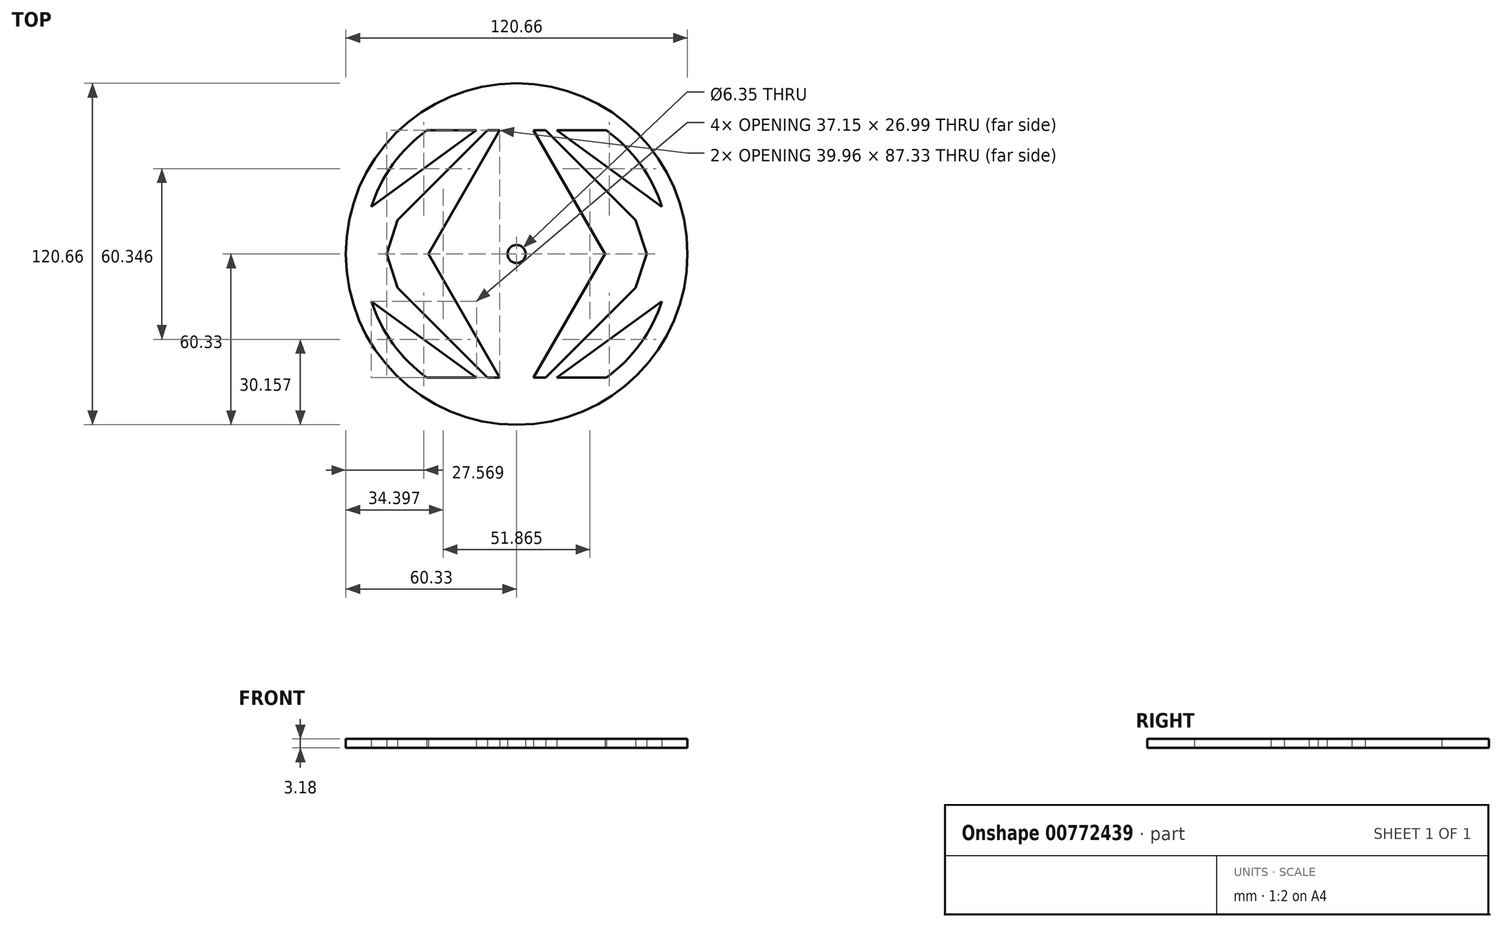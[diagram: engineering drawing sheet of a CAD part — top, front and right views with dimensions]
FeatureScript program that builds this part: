
annotation { "Feature Type Name" : "Feature", "Feature Type Description" : "" }
export const myFeature = defineFeature(function(context is Context, id is Id, definition is map)
    precondition{}
    {
        {
            var Q0;
            Q0=qCreatedBy(makeId("Top.planeOp"),FACE);
            var sketch = newSketch(context, id + "F0", { "sketchPlane" : qUnion([Q0])});
            skCircle(sketch, "E0", {"center": v(0, 0) * mm, "radius": 60.32 * mm});
            skCircle(sketch, "E1.0", {"center": v(0, 0) * mm, "radius": 53.97 * mm});
            skCircle(sketch, "E2.cCircle", {"center": v(0, 0) * mm, "radius": 53.97 * mm, "construction": true});
            skLineSegment(sketch, "E2.0", {"start": v(0, 53.97) * mm, "end": v(51.33, 16.68) * mm});
            skLineSegment(sketch, "E2.1", {"start": v(51.33, 16.68) * mm, "end": v(31.73, -43.67) * mm});
            skLineSegment(sketch, "E2.2", {"start": v(31.73, -43.67) * mm, "end": v(-31.73, -43.67) * mm});
            skLineSegment(sketch, "E2.3", {"start": v(-31.73, -43.67) * mm, "end": v(-51.33, 16.68) * mm});
            skLineSegment(sketch, "E2.4", {"start": v(-51.33, 16.68) * mm, "end": v(0, 53.97) * mm});
            skLineSegment(sketch, "E3.0", {"start": v(0, 53.97) * mm, "end": v(53.97, 0) * mm});
            skLineSegment(sketch, "E3.1", {"start": v(53.98, 0) * mm, "end": v(0, -53.97) * mm});
            skLineSegment(sketch, "E3.2", {"start": v(0, -53.97) * mm, "end": v(-53.97, 0) * mm});
            skLineSegment(sketch, "E3.3", {"start": v(-53.97, 0) * mm, "end": v(0, 53.97) * mm});
            skLineSegment(sketch, "E4.0", {"start": v(0, 53.97) * mm, "end": v(46.74, -26.99) * mm});
            skLineSegment(sketch, "E4.1", {"start": v(46.74, -26.99) * mm, "end": v(-46.74, -26.99) * mm});
            skLineSegment(sketch, "E4.2", {"start": v(-46.74, -26.99) * mm, "end": v(0, 53.98) * mm});
            skLineSegment(sketch, "E5.0", {"start": v(0, -53.97) * mm, "end": v(-51.33, -16.68) * mm});
            skLineSegment(sketch, "E5.1", {"start": v(-51.33, -16.68) * mm, "end": v(-31.73, 43.67) * mm});
            skLineSegment(sketch, "E5.2", {"start": v(-31.73, 43.67) * mm, "end": v(31.73, 43.67) * mm});
            skLineSegment(sketch, "E5.3", {"start": v(31.73, 43.67) * mm, "end": v(51.33, -16.68) * mm});
            skLineSegment(sketch, "E5.4", {"start": v(51.33, -16.68) * mm, "end": v(0, -53.97) * mm});
            skLineSegment(sketch, "E6.1", {"start": v(-53.98, 0) * mm, "end": v(0, 53.98) * mm});
            skLineSegment(sketch, "E6.3", {"start": v(53.97, 0) * mm, "end": v(0, -53.97) * mm});
            skLineSegment(sketch, "E7.0", {"start": v(0, -53.97) * mm, "end": v(-46.74, 26.99) * mm});
            skLineSegment(sketch, "E7.1", {"start": v(-46.74, 26.99) * mm, "end": v(46.74, 26.99) * mm});
            skLineSegment(sketch, "E7.2", {"start": v(46.74, 26.99) * mm, "end": v(0, -53.97) * mm});
            skCircle(sketch, "E8", {"center": v(0, 0) * mm, "radius": 3.18 * mm});
            skSolve(sketch);
        }
        {
            var Q0;
            Q0=makeQuery(id+"F0.imprint","IMPRINT",FACE,{"disambiguationData":[TD([[makeQuery(id+"F0.imprint","IMPRINT",EDGE,{"derivedFrom":sQuery(id+"F0.wireOp",EDGE,"E0")}),1.0]])]});
            var Q1;
            {var subQ0=sQuery(id+"F0.wireOp",EDGE,"E5.2");var subQ1=sQuery(id+"F0.wireOp",EDGE,"E2.0");var subQ2=makeQuery(id+"F0.imprint","INTERSECT",VERTEX,{"derivedFrom":[subQ1,subQ0]});Q1=makeQuery(id+"F0.imprint","IMPRINT",FACE,{"disambiguationData":[TD([[makeQuery(id+"F0.imprint","IMPRINT",EDGE,{"disambiguationData":[TD([[subQ2,1.0]])],"derivedFrom":subQ0}),-1.0]])]});}
            var Q2;
            {var subQ1=sQuery(id+"F0.wireOp",EDGE,"E2.0");var subQ3=sQuery(id+"F0.wireOp",EDGE,"E5.2");var subQ4=makeQuery(id+"F0.imprint","INTERSECT",VERTEX,{"derivedFrom":[subQ1,subQ3]});Q2=makeQuery(id+"F0.imprint","IMPRINT",FACE,{"disambiguationData":[TD([[makeQuery(id+"F0.imprint","IMPRINT",EDGE,{"disambiguationData":[TD([[subQ4,1.0]])],"derivedFrom":subQ3}),1.0]])]});}
            var Q3;
            {var subQ3=sQuery(id+"F0.wireOp",EDGE,"E7.1");var subQ5=sQuery(id+"F0.wireOp",EDGE,"E3.0");var subQ6=makeQuery(id+"F0.imprint","INTERSECT",VERTEX,{"derivedFrom":[subQ5,subQ3]});Q3=makeQuery(id+"F0.imprint","IMPRINT",FACE,{"disambiguationData":[TD([[makeQuery(id+"F0.imprint","IMPRINT",EDGE,{"disambiguationData":[TD([[subQ6,-1.0]])],"derivedFrom":subQ5}),1.0]])]});}
            var Q4;
            {var subQ0=sQuery(id+"F0.wireOp",EDGE,"E7.2");var subQ1=sQuery(id+"F0.wireOp",EDGE,"E2.0");var subQ2=makeQuery(id+"F0.imprint","INTERSECT",VERTEX,{"derivedFrom":[subQ1,subQ0]});Q4=makeQuery(id+"F0.imprint","IMPRINT",FACE,{"disambiguationData":[TD([[makeQuery(id+"F0.imprint","IMPRINT",EDGE,{"disambiguationData":[TD([[subQ2,-1.0]])],"derivedFrom":subQ0}),-1.0]])]});}
            var Q5;
            {var subQ0=sQuery(id+"F0.wireOp",EDGE,"E7.2");var subQ1=sQuery(id+"F0.wireOp",EDGE,"E5.3");var subQ2=makeQuery(id+"F0.imprint","INTERSECT",VERTEX,{"derivedFrom":[subQ1,subQ0]});Q5=makeQuery(id+"F0.imprint","IMPRINT",FACE,{"disambiguationData":[TD([[makeQuery(id+"F0.imprint","IMPRINT",EDGE,{"disambiguationData":[TD([[subQ2,-1.0]])],"derivedFrom":subQ1}),-1.0]])]});}
            var Q6;
            {var subQ3=sQuery(id+"F0.wireOp",EDGE,"E5.3");var subQ7=sQuery(id+"F0.wireOp",EDGE,"E7.2");var subQ9=makeQuery(id+"F0.imprint","INTERSECT",VERTEX,{"derivedFrom":[subQ3,subQ7]});Q6=makeQuery(id+"F0.imprint","IMPRINT",FACE,{"disambiguationData":[TD([[makeQuery(id+"F0.imprint","IMPRINT",EDGE,{"disambiguationData":[TD([[subQ9,-1.0]])],"derivedFrom":subQ3}),1.0]])]});}
            var Q7;
            {var subQ0=sQuery(id+"F0.wireOp",EDGE,"E2.1");var subQ3=sQuery(id+"F0.wireOp",EDGE,"E3.0");var subQ5=makeQuery(id+"F0.imprint","INTERSECT",VERTEX,{"derivedFrom":[subQ0,subQ3]});Q7=makeQuery(id+"F0.imprint","IMPRINT",FACE,{"disambiguationData":[TD([[makeQuery(id+"F0.imprint","IMPRINT",EDGE,{"disambiguationData":[TD([[subQ5,1.0]])],"derivedFrom":subQ0}),1.0]])]});}
            var Q8;
            {var subQ0=sQuery(id+"F0.wireOp",EDGE,"E3.0");var subQ1=sQuery(id+"F0.wireOp",EDGE,"E2.1");var subQ2=makeQuery(id+"F0.imprint","INTERSECT",VERTEX,{"derivedFrom":[subQ1,subQ0]});Q8=makeQuery(id+"F0.imprint","IMPRINT",FACE,{"disambiguationData":[TD([[makeQuery(id+"F0.imprint","IMPRINT",EDGE,{"disambiguationData":[TD([[subQ2,-1.0]])],"derivedFrom":subQ1}),1.0]])]});}
            var Q9;
            {var subQ0=sQuery(id+"F0.wireOp",EDGE,"E5.3");var subQ3=sQuery(id+"F0.wireOp",EDGE,"E6.3");var subQ5=makeQuery(id+"F0.imprint","INTERSECT",VERTEX,{"derivedFrom":[subQ0,subQ3]});Q9=makeQuery(id+"F0.imprint","IMPRINT",FACE,{"disambiguationData":[TD([[makeQuery(id+"F0.imprint","IMPRINT",EDGE,{"disambiguationData":[TD([[subQ5,-1.0]])],"derivedFrom":subQ0}),1.0]])]});}
            var Q10;
            {var subQ5=sQuery(id+"F0.wireOp",EDGE,"E6.3");var subQ7=sQuery(id+"F0.wireOp",EDGE,"E2.1");var subQ9=makeQuery(id+"F0.imprint","INTERSECT",VERTEX,{"derivedFrom":[subQ7,subQ5]});Q10=makeQuery(id+"F0.imprint","IMPRINT",FACE,{"disambiguationData":[TD([[makeQuery(id+"F0.imprint","IMPRINT",EDGE,{"disambiguationData":[TD([[subQ9,-1.0]])],"derivedFrom":subQ7}),1.0]])]});}
            var Q11;
            {var subQ0=sQuery(id+"F0.wireOp",EDGE,"E4.0");var subQ1=sQuery(id+"F0.wireOp",EDGE,"E2.1");var subQ2=makeQuery(id+"F0.imprint","INTERSECT",VERTEX,{"derivedFrom":[subQ1,subQ0]});Q11=makeQuery(id+"F0.imprint","IMPRINT",FACE,{"disambiguationData":[TD([[makeQuery(id+"F0.imprint","IMPRINT",EDGE,{"disambiguationData":[TD([[subQ2,-1.0]])],"derivedFrom":subQ0}),-1.0]])]});}
            var Q12;
            {var subQ0=sQuery(id+"F0.wireOp",EDGE,"E4.0");var subQ1=sQuery(id+"F0.wireOp",EDGE,"E2.1");var subQ2=makeQuery(id+"F0.imprint","INTERSECT",VERTEX,{"derivedFrom":[subQ1,subQ0]});Q12=makeQuery(id+"F0.imprint","IMPRINT",FACE,{"disambiguationData":[TD([[makeQuery(id+"F0.imprint","IMPRINT",EDGE,{"disambiguationData":[TD([[subQ2,1.0]])],"derivedFrom":subQ0}),-1.0]])]});}
            var Q13;
            {var subQ0=sQuery(id+"F0.wireOp",EDGE,"E5.4");var subQ1=sQuery(id+"F0.wireOp",EDGE,"E2.2");var subQ2=makeQuery(id+"F0.imprint","INTERSECT",VERTEX,{"derivedFrom":[subQ1,subQ0]});Q13=makeQuery(id+"F0.imprint","IMPRINT",FACE,{"disambiguationData":[TD([[makeQuery(id+"F0.imprint","IMPRINT",EDGE,{"disambiguationData":[TD([[subQ2,-1.0]])],"derivedFrom":subQ1}),-1.0]])]});}
            var Q14;
            {var subQ0=sQuery(id+"F0.wireOp",EDGE,"E5.4");var subQ1=sQuery(id+"F0.wireOp",EDGE,"E2.2");var subQ2=makeQuery(id+"F0.imprint","INTERSECT",VERTEX,{"derivedFrom":[subQ1,subQ0]});Q14=makeQuery(id+"F0.imprint","IMPRINT",FACE,{"disambiguationData":[TD([[makeQuery(id+"F0.imprint","IMPRINT",EDGE,{"disambiguationData":[TD([[subQ2,-1.0]])],"derivedFrom":subQ1}),1.0]])]});}
            var Q15;
            {var subQ0=sQuery(id+"F0.wireOp",EDGE,"E6.3");var subQ1=sQuery(id+"F0.wireOp",EDGE,"E2.1");var subQ2=makeQuery(id+"F0.imprint","INTERSECT",VERTEX,{"derivedFrom":[subQ1,subQ0]});Q15=makeQuery(id+"F0.imprint","IMPRINT",FACE,{"disambiguationData":[TD([[makeQuery(id+"F0.imprint","IMPRINT",EDGE,{"disambiguationData":[TD([[subQ2,-1.0]])],"derivedFrom":subQ1}),-1.0]])]});}
            var Q16;
            {var subQ0=sQuery(id+"F0.wireOp",EDGE,"E3.0");var subQ1=sQuery(id+"F0.wireOp",EDGE,"E2.1");var subQ2=makeQuery(id+"F0.imprint","INTERSECT",VERTEX,{"derivedFrom":[subQ1,subQ0]});Q16=makeQuery(id+"F0.imprint","IMPRINT",FACE,{"disambiguationData":[TD([[makeQuery(id+"F0.imprint","IMPRINT",EDGE,{"disambiguationData":[TD([[subQ2,-1.0]])],"derivedFrom":subQ1}),-1.0]])]});}
            var Q17;
            {var subQ0=sQuery(id+"F0.wireOp",EDGE,"E5.3");var subQ1=sQuery(id+"F0.wireOp",EDGE,"E2.1");var subQ2=makeQuery(id+"F0.imprint","INTERSECT",VERTEX,{"derivedFrom":[subQ1,subQ0]});Q17=makeQuery(id+"F0.imprint","IMPRINT",FACE,{"disambiguationData":[TD([[makeQuery(id+"F0.imprint","IMPRINT",EDGE,{"disambiguationData":[TD([[subQ2,-1.0]])],"derivedFrom":subQ1}),1.0]])]});}
            var Q18;
            {var subQ1=sQuery(id+"F0.wireOp",EDGE,"E2.4");var subQ3=sQuery(id+"F0.wireOp",EDGE,"E5.2");var subQ4=makeQuery(id+"F0.imprint","INTERSECT",VERTEX,{"derivedFrom":[subQ1,subQ3]});Q18=makeQuery(id+"F0.imprint","IMPRINT",FACE,{"disambiguationData":[TD([[makeQuery(id+"F0.imprint","IMPRINT",EDGE,{"disambiguationData":[TD([[subQ4,-1.0]])],"derivedFrom":subQ3}),1.0]])]});}
            var Q19;
            {var subQ0=sQuery(id+"F0.wireOp",EDGE,"E5.2");var subQ1=sQuery(id+"F0.wireOp",EDGE,"E2.4");var subQ2=makeQuery(id+"F0.imprint","INTERSECT",VERTEX,{"derivedFrom":[subQ1,subQ0]});Q19=makeQuery(id+"F0.imprint","IMPRINT",FACE,{"disambiguationData":[TD([[makeQuery(id+"F0.imprint","IMPRINT",EDGE,{"disambiguationData":[TD([[subQ2,-1.0]])],"derivedFrom":subQ0}),-1.0]])]});}
            var Q20;
            {var subQ0=sQuery(id+"F0.wireOp",EDGE,"E7.0");var subQ5=sQuery(id+"F0.wireOp",EDGE,"E6.1");var subQ6=makeQuery(id+"F0.imprint","INTERSECT",VERTEX,{"derivedFrom":[subQ5,subQ0]});Q20=makeQuery(id+"F0.imprint","IMPRINT",FACE,{"disambiguationData":[TD([[makeQuery(id+"F0.imprint","IMPRINT",EDGE,{"disambiguationData":[TD([[subQ6,-1.0]])],"derivedFrom":subQ5}),1.0]])]});}
            var Q21;
            {var subQ0=sQuery(id+"F0.wireOp",EDGE,"E7.0");var subQ1=sQuery(id+"F0.wireOp",EDGE,"E2.4");var subQ2=makeQuery(id+"F0.imprint","INTERSECT",VERTEX,{"derivedFrom":[subQ1,subQ0]});Q21=makeQuery(id+"F0.imprint","IMPRINT",FACE,{"disambiguationData":[TD([[makeQuery(id+"F0.imprint","IMPRINT",EDGE,{"disambiguationData":[TD([[subQ2,1.0]])],"derivedFrom":subQ0}),-1.0]])]});}
            var Q22;
            {var subQ0=sQuery(id+"F0.wireOp",EDGE,"E6.1");var subQ1=sQuery(id+"F0.wireOp",EDGE,"E5.1");var subQ2=makeQuery(id+"F0.imprint","INTERSECT",VERTEX,{"derivedFrom":[subQ1,subQ0]});Q22=makeQuery(id+"F0.imprint","IMPRINT",FACE,{"disambiguationData":[TD([[makeQuery(id+"F0.imprint","IMPRINT",EDGE,{"disambiguationData":[TD([[subQ2,-1.0]])],"derivedFrom":subQ1}),1.0]])]});}
            var Q23;
            {var subQ0=sQuery(id+"F0.wireOp",EDGE,"E6.1");var subQ1=sQuery(id+"F0.wireOp",EDGE,"E5.1");var subQ2=makeQuery(id+"F0.imprint","INTERSECT",VERTEX,{"derivedFrom":[subQ1,subQ0]});Q23=makeQuery(id+"F0.imprint","IMPRINT",FACE,{"disambiguationData":[TD([[makeQuery(id+"F0.imprint","IMPRINT",EDGE,{"disambiguationData":[TD([[subQ2,-1.0]])],"derivedFrom":subQ1}),-1.0]])]});}
            var Q24;
            {var subQ0=sQuery(id+"F0.wireOp",EDGE,"E5.1");var subQ1=sQuery(id+"F0.wireOp",EDGE,"E2.3");var subQ2=makeQuery(id+"F0.imprint","INTERSECT",VERTEX,{"derivedFrom":[subQ1,subQ0]});Q24=makeQuery(id+"F0.imprint","IMPRINT",FACE,{"disambiguationData":[TD([[makeQuery(id+"F0.imprint","IMPRINT",EDGE,{"disambiguationData":[TD([[subQ2,-1.0]])],"derivedFrom":subQ1}),-1.0]])]});}
            var Q25;
            {var subQ0=sQuery(id+"F0.wireOp",EDGE,"E5.1");var subQ1=sQuery(id+"F0.wireOp",EDGE,"E2.3");var subQ2=makeQuery(id+"F0.imprint","INTERSECT",VERTEX,{"derivedFrom":[subQ1,subQ0]});Q25=makeQuery(id+"F0.imprint","IMPRINT",FACE,{"disambiguationData":[TD([[makeQuery(id+"F0.imprint","IMPRINT",EDGE,{"disambiguationData":[TD([[subQ2,-1.0]])],"derivedFrom":subQ1}),1.0]])]});}
            var Q26;
            {var subQ0=sQuery(id+"F0.wireOp",EDGE,"E3.2");var subQ1=sQuery(id+"F0.wireOp",EDGE,"E2.3");var subQ2=makeQuery(id+"F0.imprint","INTERSECT",VERTEX,{"derivedFrom":[subQ1,subQ0]});Q26=makeQuery(id+"F0.imprint","IMPRINT",FACE,{"disambiguationData":[TD([[makeQuery(id+"F0.imprint","IMPRINT",EDGE,{"disambiguationData":[TD([[subQ2,-1.0]])],"derivedFrom":subQ1}),1.0]])]});}
            var Q27;
            {var subQ0=sQuery(id+"F0.wireOp",EDGE,"E2.3");var subQ3=sQuery(id+"F0.wireOp",EDGE,"E6.1");var subQ5=makeQuery(id+"F0.imprint","INTERSECT",VERTEX,{"derivedFrom":[subQ0,subQ3]});Q27=makeQuery(id+"F0.imprint","IMPRINT",FACE,{"disambiguationData":[TD([[makeQuery(id+"F0.imprint","IMPRINT",EDGE,{"disambiguationData":[TD([[subQ5,-1.0]])],"derivedFrom":subQ0}),1.0]])]});}
            var Q28;
            {var subQ0=sQuery(id+"F0.wireOp",EDGE,"E3.2");var subQ1=sQuery(id+"F0.wireOp",EDGE,"E2.2");var subQ2=makeQuery(id+"F0.imprint","INTERSECT",VERTEX,{"derivedFrom":[subQ1,subQ0]});Q28=makeQuery(id+"F0.imprint","IMPRINT",FACE,{"disambiguationData":[TD([[makeQuery(id+"F0.imprint","IMPRINT",EDGE,{"disambiguationData":[TD([[subQ2,-1.0]])],"derivedFrom":subQ1}),-1.0]])]});}
            var Q29;
            {var subQ0=sQuery(id+"F0.wireOp",EDGE,"E3.2");var subQ1=sQuery(id+"F0.wireOp",EDGE,"E2.2");var subQ2=makeQuery(id+"F0.imprint","INTERSECT",VERTEX,{"derivedFrom":[subQ1,subQ0]});Q29=makeQuery(id+"F0.imprint","IMPRINT",FACE,{"disambiguationData":[TD([[makeQuery(id+"F0.imprint","IMPRINT",EDGE,{"disambiguationData":[TD([[subQ2,-1.0]])],"derivedFrom":subQ1}),1.0]])]});}
            var Q30;
            {var subQ3=sQuery(id+"F0.wireOp",EDGE,"E4.2");var subQ7=sQuery(id+"F0.wireOp",EDGE,"E2.3");var subQ8=makeQuery(id+"F0.imprint","INTERSECT",VERTEX,{"derivedFrom":[subQ7,subQ3]});Q30=makeQuery(id+"F0.imprint","IMPRINT",FACE,{"disambiguationData":[TD([[makeQuery(id+"F0.imprint","IMPRINT",EDGE,{"disambiguationData":[TD([[subQ8,-1.0]])],"derivedFrom":subQ7}),1.0]])]});}
            var Q31;
            {var subQ0=sQuery(id+"F0.wireOp",EDGE,"E5.1");var subQ3=sQuery(id+"F0.wireOp",EDGE,"E3.2");var subQ5=makeQuery(id+"F0.imprint","INTERSECT",VERTEX,{"derivedFrom":[subQ0,subQ3]});Q31=makeQuery(id+"F0.imprint","IMPRINT",FACE,{"disambiguationData":[TD([[makeQuery(id+"F0.imprint","IMPRINT",EDGE,{"disambiguationData":[TD([[subQ5,1.0]])],"derivedFrom":subQ0}),1.0]])]});}
            var Q32;
            {var subQ0=sQuery(id+"F0.wireOp",EDGE,"E4.2");var subQ1=sQuery(id+"F0.wireOp",EDGE,"E2.3");var subQ2=makeQuery(id+"F0.imprint","INTERSECT",VERTEX,{"derivedFrom":[subQ1,subQ0]});Q32=makeQuery(id+"F0.imprint","IMPRINT",FACE,{"disambiguationData":[TD([[makeQuery(id+"F0.imprint","IMPRINT",EDGE,{"disambiguationData":[TD([[subQ2,1.0]])],"derivedFrom":subQ0}),-1.0]])]});}
            var Q33;
            {var subQ0=sQuery(id+"F0.wireOp",EDGE,"E4.2");var subQ1=sQuery(id+"F0.wireOp",EDGE,"E2.3");var subQ2=makeQuery(id+"F0.imprint","INTERSECT",VERTEX,{"derivedFrom":[subQ1,subQ0]});Q33=makeQuery(id+"F0.imprint","IMPRINT",FACE,{"disambiguationData":[TD([[makeQuery(id+"F0.imprint","IMPRINT",EDGE,{"disambiguationData":[TD([[subQ2,-1.0]])],"derivedFrom":subQ0}),-1.0]])]});}
            var Q34;
            {var subQ0=sQuery(id+"F0.wireOp",EDGE,"E4.2");var subQ1=sQuery(id+"F0.wireOp",EDGE,"E2.3");var subQ2=makeQuery(id+"F0.imprint","INTERSECT",VERTEX,{"derivedFrom":[subQ1,subQ0]});Q34=makeQuery(id+"F0.imprint","IMPRINT",FACE,{"disambiguationData":[TD([[makeQuery(id+"F0.imprint","IMPRINT",EDGE,{"disambiguationData":[TD([[subQ2,-1.0]])],"derivedFrom":subQ1}),-1.0]])]});}
            var Q35;
            {var subQ0=sQuery(id+"F0.wireOp",EDGE,"E2.2");var subQ3=sQuery(id+"F0.wireOp",EDGE,"E5.4");var subQ5=makeQuery(id+"F0.imprint","INTERSECT",VERTEX,{"derivedFrom":[subQ0,subQ3]});Q35=makeQuery(id+"F0.imprint","IMPRINT",FACE,{"disambiguationData":[TD([[makeQuery(id+"F0.imprint","IMPRINT",EDGE,{"disambiguationData":[TD([[subQ5,1.0]])],"derivedFrom":subQ0}),1.0]])]});}
            var Q36;
            {var subQ0=sQuery(id+"F0.wireOp",EDGE,"E2.2");var subQ3=sQuery(id+"F0.wireOp",EDGE,"E5.0");var subQ5=makeQuery(id+"F0.imprint","INTERSECT",VERTEX,{"derivedFrom":[subQ0,subQ3]});Q36=makeQuery(id+"F0.imprint","IMPRINT",FACE,{"disambiguationData":[TD([[makeQuery(id+"F0.imprint","IMPRINT",EDGE,{"disambiguationData":[TD([[subQ5,-1.0]])],"derivedFrom":subQ0}),1.0]])]});}
            var Q37;
            {var subQ0=sQuery(id+"F0.wireOp",EDGE,"E2.4");var subQ3=sQuery(id+"F0.wireOp",EDGE,"E5.2");var subQ5=makeQuery(id+"F0.imprint","INTERSECT",VERTEX,{"derivedFrom":[subQ0,subQ3]});Q37=makeQuery(id+"F0.imprint","IMPRINT",FACE,{"disambiguationData":[TD([[makeQuery(id+"F0.imprint","IMPRINT",EDGE,{"disambiguationData":[TD([[subQ5,1.0]])],"derivedFrom":subQ3}),1.0]])]});}
            var Q38;
            {var subQ0=sQuery(id+"F0.wireOp",EDGE,"E2.0");var subQ3=sQuery(id+"F0.wireOp",EDGE,"E5.2");var subQ5=makeQuery(id+"F0.imprint","INTERSECT",VERTEX,{"derivedFrom":[subQ0,subQ3]});Q38=makeQuery(id+"F0.imprint","IMPRINT",FACE,{"disambiguationData":[TD([[makeQuery(id+"F0.imprint","IMPRINT",EDGE,{"disambiguationData":[TD([[subQ5,-1.0]])],"derivedFrom":subQ3}),1.0]])]});}
            extrude(context, id + "F1", {"entities" : qUnion([Q0, Q1, Q2, Q3, Q4, Q5, Q6, Q7, Q8, Q9, Q10, Q11, Q12, Q13, Q14, Q15, Q16, Q17, Q18, Q19, Q20, Q21, Q22, Q23, Q24, Q25, Q26, Q27, Q28, Q29, Q30, Q31, Q32, Q33, Q34, Q35, Q36, Q37, Q38]), "depth" : 3.17 * mm, "offsetDistance" : 25 * mm});
        }
        {
            var Q0;
            {var subQ1=sQuery(id+"F0.wireOp",EDGE,"E4.0");var subQ3=sQuery(id+"F0.wireOp",EDGE,"E5.2");var subQ4=makeQuery(id+"F0.imprint","INTERSECT",VERTEX,{"derivedFrom":[subQ1,subQ3]});Q0=makeQuery(id+"F0.imprint","IMPRINT",FACE,{"disambiguationData":[TD([[makeQuery(id+"F0.imprint","IMPRINT",EDGE,{"disambiguationData":[TD([[subQ4,1.0]])],"derivedFrom":subQ3}),1.0]])]});}
            var Q1;
            {var subQ0=sQuery(id+"F0.wireOp",EDGE,"E5.2");var subQ1=sQuery(id+"F0.wireOp",EDGE,"E4.0");var subQ2=makeQuery(id+"F0.imprint","INTERSECT",VERTEX,{"derivedFrom":[subQ1,subQ0]});Q1=makeQuery(id+"F0.imprint","IMPRINT",FACE,{"disambiguationData":[TD([[makeQuery(id+"F0.imprint","IMPRINT",EDGE,{"disambiguationData":[TD([[subQ2,-1.0]])],"derivedFrom":subQ1}),-1.0]])]});}
            var Q2;
            {var subQ5=sQuery(id+"F0.wireOp",EDGE,"E7.1");var subQ9=sQuery(id+"F0.wireOp",EDGE,"E4.0");var subQ10=makeQuery(id+"F0.imprint","INTERSECT",VERTEX,{"derivedFrom":[subQ9,subQ5]});Q2=makeQuery(id+"F0.imprint","IMPRINT",FACE,{"disambiguationData":[TD([[makeQuery(id+"F0.imprint","IMPRINT",EDGE,{"disambiguationData":[TD([[subQ10,-1.0]])],"derivedFrom":subQ9}),-1.0]])]});}
            var Q3;
            {var subQ0=sQuery(id+"F0.wireOp",EDGE,"E7.2");var subQ1=sQuery(id+"F0.wireOp",EDGE,"E2.2");var subQ2=makeQuery(id+"F0.imprint","INTERSECT",VERTEX,{"derivedFrom":[subQ1,subQ0]});Q3=makeQuery(id+"F0.imprint","IMPRINT",FACE,{"disambiguationData":[TD([[makeQuery(id+"F0.imprint","IMPRINT",EDGE,{"disambiguationData":[TD([[subQ2,-1.0]])],"derivedFrom":subQ1}),1.0]])]});}
            var Q4;
            {var subQ0=sQuery(id+"F0.wireOp",EDGE,"E7.2");var subQ1=sQuery(id+"F0.wireOp",EDGE,"E2.2");var subQ2=makeQuery(id+"F0.imprint","INTERSECT",VERTEX,{"derivedFrom":[subQ1,subQ0]});Q4=makeQuery(id+"F0.imprint","IMPRINT",FACE,{"disambiguationData":[TD([[makeQuery(id+"F0.imprint","IMPRINT",EDGE,{"disambiguationData":[TD([[subQ2,-1.0]])],"derivedFrom":subQ1}),-1.0]])]});}
            var Q5;
            {var subQ0=sQuery(id+"F0.wireOp",EDGE,"E6.3");var subQ1=sQuery(id+"F0.wireOp",EDGE,"E2.2");var subQ2=makeQuery(id+"F0.imprint","INTERSECT",VERTEX,{"derivedFrom":[subQ1,subQ0]});Q5=makeQuery(id+"F0.imprint","IMPRINT",FACE,{"disambiguationData":[TD([[makeQuery(id+"F0.imprint","IMPRINT",EDGE,{"disambiguationData":[TD([[subQ2,-1.0]])],"derivedFrom":subQ1}),1.0]])]});}
            var Q6;
            {var subQ0=sQuery(id+"F0.wireOp",EDGE,"E7.0");var subQ1=sQuery(id+"F0.wireOp",EDGE,"E2.2");var subQ2=makeQuery(id+"F0.imprint","INTERSECT",VERTEX,{"derivedFrom":[subQ1,subQ0]});Q6=makeQuery(id+"F0.imprint","IMPRINT",FACE,{"disambiguationData":[TD([[makeQuery(id+"F0.imprint","IMPRINT",EDGE,{"disambiguationData":[TD([[subQ2,-1.0]])],"derivedFrom":subQ1}),1.0]])]});}
            var Q7;
            {var subQ1=sQuery(id+"F0.wireOp",EDGE,"E4.2");var subQ3=sQuery(id+"F0.wireOp",EDGE,"E5.2");var subQ4=makeQuery(id+"F0.imprint","INTERSECT",VERTEX,{"derivedFrom":[subQ1,subQ3]});Q7=makeQuery(id+"F0.imprint","IMPRINT",FACE,{"disambiguationData":[TD([[makeQuery(id+"F0.imprint","IMPRINT",EDGE,{"disambiguationData":[TD([[subQ4,1.0]])],"derivedFrom":subQ3}),1.0]])]});}
            var Q8;
            {var subQ1=sQuery(id+"F0.wireOp",EDGE,"E4.0");var subQ3=sQuery(id+"F0.wireOp",EDGE,"E5.2");var subQ4=makeQuery(id+"F0.imprint","INTERSECT",VERTEX,{"derivedFrom":[subQ1,subQ3]});Q8=makeQuery(id+"F0.imprint","IMPRINT",FACE,{"disambiguationData":[TD([[makeQuery(id+"F0.imprint","IMPRINT",EDGE,{"disambiguationData":[TD([[subQ4,-1.0]])],"derivedFrom":subQ3}),1.0]])]});}
            extrude(context, id + "F2", {"entities" : qUnion([Q0, Q1, Q2, Q3, Q4, Q5, Q6, Q7, Q8]), "operationType" : NewBodyOperationType.ADD, "depth" : 3.17 * mm, "offsetDistance" : 25 * mm});
        }
    });
